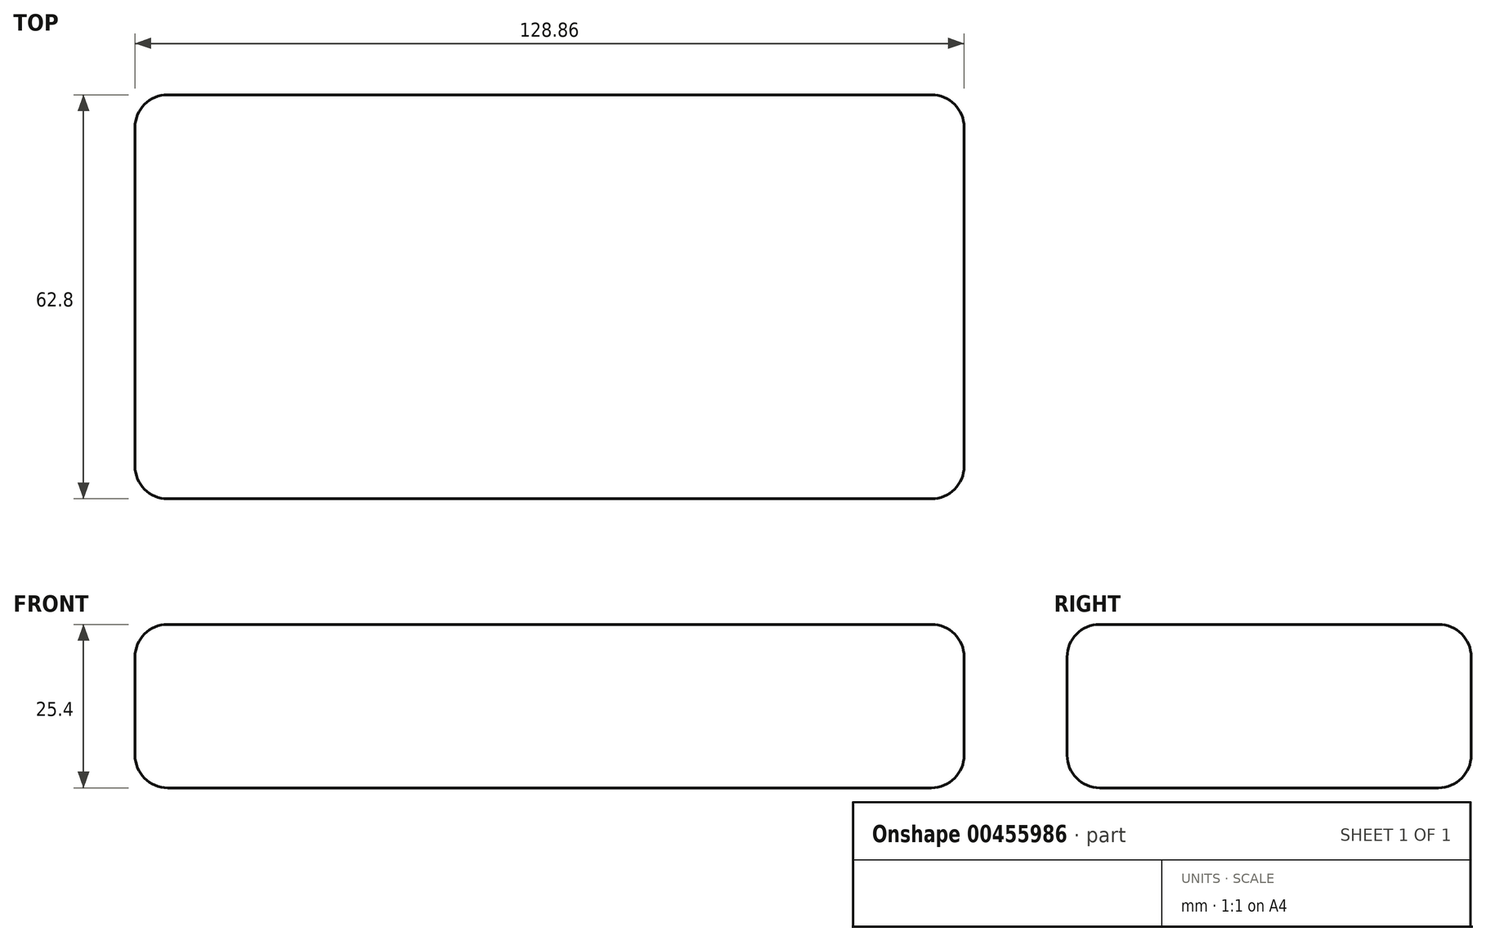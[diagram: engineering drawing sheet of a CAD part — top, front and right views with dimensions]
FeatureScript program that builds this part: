
annotation { "Feature Type Name" : "Feature", "Feature Type Description" : "" }
export const myFeature = defineFeature(function(context is Context, id is Id, definition is map)
    precondition{}
    {
        {
            var Q0;
            Q0=qCreatedBy(makeId("Top.planeOp"),FACE);
            var sketch = newSketch(context, id + "F0", { "sketchPlane" : qUnion([Q0])});
            skLineSegment(sketch, "E0.bottom", {"start": v(-64.43, 31.4) * mm, "end": v(64.43, 31.4) * mm});
            skLineSegment(sketch, "E0.top", {"start": v(-64.43, -31.4) * mm, "end": v(64.43, -31.4) * mm});
            skLineSegment(sketch, "E0.left", {"start": v(-64.43, 31.4) * mm, "end": v(-64.43, -31.4) * mm});
            skLineSegment(sketch, "E0.right", {"start": v(64.43, 31.4) * mm, "end": v(64.43, -31.4) * mm});
            skPoint(sketch, "E0.middle", {"position": v(0, 0) * mm});
            skSolve(sketch);
        }
        {
            var Q0;
            Q0=makeQuery(id+"F0.imprint","IMPRINT",FACE,{"disambiguationData":[TD([[makeQuery(id+"F0.imprint","IMPRINT",EDGE,{"derivedFrom":sQuery(id+"F0.wireOp",EDGE,"E0.bottom")}),-1.0]])]});
            extrude(context, id + "F1", {"entities" : qUnion([Q0]), "depth" : 25.4 * mm});
        }
        {
            var Q0;
            Q0=makeQuery(id+"F1.opExtrude","CAP_FACE",FACE,{"disambiguationData":[OSD([sQuery(id+"F0.wireOp",EDGE,"E0.bottom"),sQuery(id+"F0.wireOp",EDGE,"E0.top"),sQuery(id+"F0.wireOp",EDGE,"E0.left"),sQuery(id+"F0.wireOp",EDGE,"E0.right")])],"isStart":true});
            var Q1;
            Q1=makeQuery(id+"F1.opExtrude","CAP_EDGE",EDGE,{"disambiguationData":[OSD([sQuery(id+"F0.wireOp",EDGE,"E0.right")])],"isStart":true});
            var Q2;
            Q2=makeQuery(id+"F1.opExtrude","CAP_EDGE",EDGE,{"disambiguationData":[OSD([sQuery(id+"F0.wireOp",EDGE,"E0.right")])],"isStart":false});
            var Q3;
            Q3=makeQuery(id+"F1.opExtrude","CAP_EDGE",EDGE,{"disambiguationData":[OSD([sQuery(id+"F0.wireOp",EDGE,"E0.left")])],"isStart":false});
            var Q4;
            Q4=makeQuery(id+"F1.opExtrude","CAP_EDGE",EDGE,{"disambiguationData":[OSD([sQuery(id+"F0.wireOp",EDGE,"E0.top")])],"isStart":false});
            var Q5;
            Q5=makeQuery(id+"F1.opExtrude","CAP_EDGE",EDGE,{"disambiguationData":[OSD([sQuery(id+"F0.wireOp",EDGE,"E0.top")])],"isStart":true});
            var Q6;
            Q6=makeQuery(id+"F1.opExtrude","SWEPT_FACE",FACE,{"disambiguationData":[OSD([sQuery(id+"F0.wireOp",EDGE,"E0.right")])]});
            var Q7;
            Q7=makeQuery(id+"F1.opExtrude","SWEPT_FACE",FACE,{"disambiguationData":[OSD([sQuery(id+"F0.wireOp",EDGE,"E0.bottom")])]});
            var Q8;
            Q8=makeQuery(id+"F1.opExtrude","SWEPT_EDGE",EDGE,{"disambiguationData":[OSD([sQuery(id+"F0.wireOp",EDGE,"E0.bottom"),sQuery(id+"F0.wireOp",EDGE,"E0.right")])]});
            var Q9;
            Q9=makeQuery(id+"F1.opExtrude","CAP_FACE",FACE,{"disambiguationData":[OSD([sQuery(id+"F0.wireOp",EDGE,"E0.bottom"),sQuery(id+"F0.wireOp",EDGE,"E0.top"),sQuery(id+"F0.wireOp",EDGE,"E0.left"),sQuery(id+"F0.wireOp",EDGE,"E0.right")])],"isStart":false});
            var Q10;
            Q10=makeQuery(id+"F1.opExtrude","SWEPT_EDGE",EDGE,{"disambiguationData":[OSD([sQuery(id+"F0.wireOp",EDGE,"E0.top"),sQuery(id+"F0.wireOp",EDGE,"E0.left")])]});
            var Q11;
            Q11=makeQuery(id+"F1.opExtrude","SWEPT_FACE",FACE,{"disambiguationData":[OSD([sQuery(id+"F0.wireOp",EDGE,"E0.top")])]});
            var Q12;
            Q12=makeQuery(id+"F1.opExtrude","SWEPT_EDGE",EDGE,{"disambiguationData":[OSD([sQuery(id+"F0.wireOp",EDGE,"E0.top"),sQuery(id+"F0.wireOp",EDGE,"E0.right")])]});
            var Q13;
            Q13=makeQuery(id+"F1.opExtrude","CAP_EDGE",EDGE,{"disambiguationData":[OSD([sQuery(id+"F0.wireOp",EDGE,"E0.left")])],"isStart":true});
            var Q14;
            Q14=makeQuery(id+"F1.opExtrude","SWEPT_EDGE",EDGE,{"disambiguationData":[OSD([sQuery(id+"F0.wireOp",EDGE,"E0.bottom"),sQuery(id+"F0.wireOp",EDGE,"E0.left")])]});
            var Q15;
            Q15=makeQuery(id+"F1.opExtrude","CAP_EDGE",EDGE,{"disambiguationData":[OSD([sQuery(id+"F0.wireOp",EDGE,"E0.bottom")])],"isStart":false});
            var Q16;
            Q16=makeQuery(id+"F1.opExtrude","SWEPT_FACE",FACE,{"disambiguationData":[OSD([sQuery(id+"F0.wireOp",EDGE,"E0.left")])]});
            var Q17;
            Q17=makeQuery(id+"F1.opExtrude","CAP_EDGE",EDGE,{"disambiguationData":[OSD([sQuery(id+"F0.wireOp",EDGE,"E0.bottom")])],"isStart":true});
            fillet(context, id + "F2", {"entities" : qUnion([Q0, Q1, Q2, Q3, Q4, Q5, Q6, Q7, Q8, Q9, Q10, Q11, Q12, Q13, Q14, Q15, Q16, Q17]), "radius" : 5.08 * mm, "tangentPropagation" : true, "allowEdgeOverflow" : false});
        }
    });
